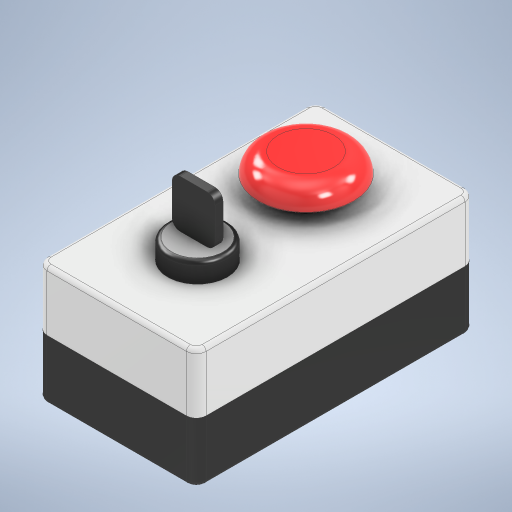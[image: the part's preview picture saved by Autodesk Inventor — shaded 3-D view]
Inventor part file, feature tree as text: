
AUTODESK INVENTOR PART (.ipt)
format: ipt  version: 2024 (Build 280153000, 153)  size: 383,488 bytes
history: native  units: in
note: dims shown in document units (in); Inventor stores cm internally (conversion verified against a paired STEP export)
features: extrude x6, sketch x6, fillet x5, projected_geometry x2
ambient origin geometry x8: Origin, YZ Plane, XZ Plane, XY Plane, X Axis, Y Axis, Z Axis, Center Point
bodies: Solid1 (feature_tree)
feature tree (19):
  extrude  "Extrusion1"  Depth=3.5in
  extrude  "Extrusion2"  Depth=0.75in TaperAngle=0.0deg
  fillet  "Fillet2"  Radius=0.001in
  extrude  "Extrusion3"  Depth=0.05in
  fillet  "Fillet3"  Radius=0.5in
  extrude  "Extrusion4"  Depth=0.25in TaperAngle=0.0deg
  fillet  "Fillet4"  Radius=0.05in
  fillet  "Fillet5"  Radius=1.2in
  extrude  "Extrusion5"  Depth=0.25in
  fillet  "Fillet6"  Radius=0.01in
  extrude  "Extrusion6"  Depth=0.05in
  sketch  "Sketch1"  dims[d0=2.0in d1=3.5in]
  sketch  "Sketch2"  dims[d2=0.125in d3=0.75in d4=0.0in d6=0.001in]
  projected_geometry  "Projected Loop1"
  sketch  "Sketch3"  dims[d7=0.75in d8=0.0in d9=0.05in d10=0.5in]
  sketch  "Sketch4"  dims[d11=0.75in d12=0.25in d13=0.0in d14=0.05in d15=1.2in]
  sketch  "Sketch5"  dims[d16=0.25in d17=0.0in d18=0.25in d19=0.01in]
  sketch  "Sketch6"  dims[d20=0.27in d21=0.05in d22=0.54in d23=0.1in d24=0.6in d25=0.0in d26=0.1in d27=0.1in d28=0.1in d29=0.1in d30=0.1in d31=0.6in d32=0.0in]
  projected_geometry  "Projected Loop2"
